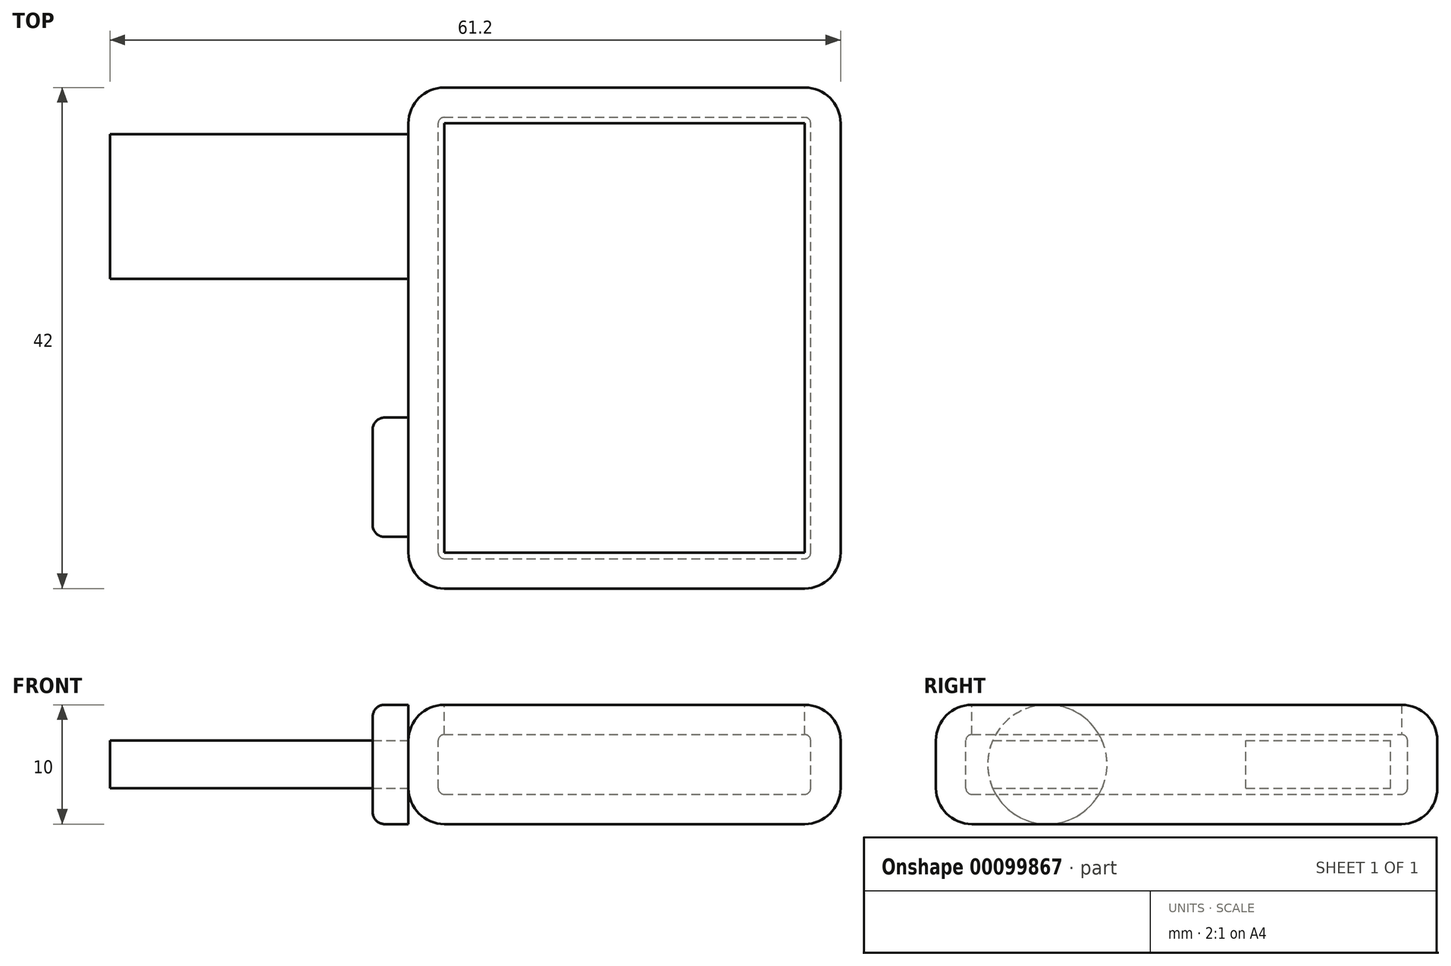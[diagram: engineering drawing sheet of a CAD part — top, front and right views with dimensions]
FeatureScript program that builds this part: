
annotation { "Feature Type Name" : "Feature", "Feature Type Description" : "" }
export const myFeature = defineFeature(function(context is Context, id is Id, definition is map)
    precondition{}
    {
        {
            var Q0;
            Q0=qCreatedBy(makeId("Top.planeOp"),FACE);
            var sketch = newSketch(context, id + "F0", { "sketchPlane" : qUnion([Q0])});
            skLineSegment(sketch, "E0.bottom", {"start": v(-18.1, -21) * mm, "end": v(18.1, -21) * mm});
            skLineSegment(sketch, "E0.top", {"start": v(-18.1, 21) * mm, "end": v(18.1, 21) * mm});
            skLineSegment(sketch, "E0.left", {"start": v(-18.1, -21) * mm, "end": v(-18.1, 21) * mm});
            skLineSegment(sketch, "E0.right", {"start": v(18.1, -21) * mm, "end": v(18.1, 21) * mm});
            skPoint(sketch, "E0.middle", {"position": v(0, 0) * mm});
            skSolve(sketch);
        }
        {
            var Q0;
            Q0=makeQuery(id+"F0.imprint","IMPRINT",FACE,{"disambiguationData":[TD([[makeQuery(id+"F0.imprint","IMPRINT",EDGE,{"derivedFrom":sQuery(id+"F0.wireOp",EDGE,"E0.bottom")}),1.0]])]});
            extrude(context, id + "F1", {"entities" : qUnion([Q0]), "depth" : 10 * mm});
        }
        {
            var Q0;
            Q0=makeQuery(id+"F1.opExtrude","SWEPT_FACE",FACE,{"disambiguationData":[OSD([sQuery(id+"F0.wireOp",EDGE,"E0.bottom")])]});
            var Q1;
            Q1=makeQuery(id+"F1.opExtrude","SWEPT_FACE",FACE,{"disambiguationData":[OSD([sQuery(id+"F0.wireOp",EDGE,"E0.left")])]});
            var Q2;
            Q2=makeQuery(id+"F1.opExtrude","SWEPT_FACE",FACE,{"disambiguationData":[OSD([sQuery(id+"F0.wireOp",EDGE,"E0.top")])]});
            var Q3;
            Q3=makeQuery(id+"F1.opExtrude","SWEPT_FACE",FACE,{"disambiguationData":[OSD([sQuery(id+"F0.wireOp",EDGE,"E0.right")])]});
            fillet(context, id + "F2", {"entities" : qUnion([Q0, Q1, Q2, Q3]), "radius" : 3 * mm, "tangentPropagation" : true, "allowEdgeOverflow" : false});
        }
        {
            var Q0;
            Q0=makeQuery(id+"F1.opExtrude","CAP_FACE",FACE,{"disambiguationData":[OSD([sQuery(id+"F0.wireOp",EDGE,"E0.bottom"),sQuery(id+"F0.wireOp",EDGE,"E0.top"),sQuery(id+"F0.wireOp",EDGE,"E0.left"),sQuery(id+"F0.wireOp",EDGE,"E0.right")])],"isStart":false});
            shell(context, id + "F3", {"entities" : qUnion([Q0]), "thickness" : 2.5 * mm});
        }
        {
            var Q0;
            Q0=makeQuery(id+"F1.opExtrude","SWEPT_FACE",FACE,{"disambiguationData":[OSD([sQuery(id+"F0.wireOp",EDGE,"E0.left")])]});
            var sketch = newSketch(context, id + "F4", { "sketchPlane" : qUnion([Q0])});
            skCircle(sketch, "E1", {"center": v(11.67, 5) * mm, "radius": 5 * mm});
            skPoint(sketch, "E1.centerSnap0", {"position": v(18, 5) * mm});
            skSolve(sketch);
        }
        {
            var Q0;
            {var subQ0=sQuery(id+"F4.wireOp",EDGE,"E1");var subQ1=sQuery(id+"F0.wireOp",EDGE,"E0.left");var subQ2=makeQuery(id+"F2.opFillet","BLEND_EDGE",EDGE,{"blendedFrom":[makeQuery(id+"F1.opExtrude","CAP_EDGE",EDGE,{"disambiguationData":[OSD([subQ1])],"isStart":true}),makeQuery(id+"F1.opExtrude","SWEPT_FACE",FACE,{"disambiguationData":[OSD([subQ1])]})],"blendedInto":[makeQuery(id+"F1.opExtrude","SWEPT_FACE",FACE,{"disambiguationData":[OSD([subQ1])]})]});var subQ3=makeQuery(id+"F4.imprint","INTERSECT",VERTEX,{"disambiguationData":[OD(0.0)],"derivedFrom":[subQ2,subQ0]});Q0=makeQuery(id+"F4.imprint","IMPRINT",FACE,{"disambiguationData":[TD([[makeQuery(id+"F4.imprint","IMPRINT",EDGE,{"disambiguationData":[TD([[subQ3,-1.0]])],"derivedFrom":subQ0}),1.0]])]});}
            var Q1;
            {var subQ0=sQuery(id+"F4.wireOp",EDGE,"E1");var subQ1=sQuery(id+"F0.wireOp",EDGE,"E0.left");var subQ2=makeQuery(id+"F1.opExtrude","SWEPT_FACE",FACE,{"disambiguationData":[OSD([subQ1])]});var subQ3=makeQuery(id+"F2.opFillet","BLEND_EDGE",EDGE,{"blendedFrom":[makeQuery(id+"F1.opExtrude","CAP_EDGE",EDGE,{"disambiguationData":[OSD([subQ1])],"isStart":false}),subQ2],"blendedInto":[subQ2]});var subQ4=makeQuery(id+"F4.imprint","INTERSECT",VERTEX,{"disambiguationData":[OD(0.0)],"derivedFrom":[subQ3,subQ0]});Q1=makeQuery(id+"F4.imprint","IMPRINT",FACE,{"disambiguationData":[TD([[makeQuery(id+"F4.imprint","IMPRINT",EDGE,{"disambiguationData":[TD([[subQ4,-1.0]])],"derivedFrom":subQ0}),1.0]])]});}
            var Q2;
            {var subQ0=sQuery(id+"F4.wireOp",EDGE,"E1");var subQ1=sQuery(id+"F0.wireOp",EDGE,"E0.left");var subQ2=makeQuery(id+"F2.opFillet","BLEND_EDGE",EDGE,{"blendedFrom":[makeQuery(id+"F1.opExtrude","CAP_EDGE",EDGE,{"disambiguationData":[OSD([subQ1])],"isStart":false}),makeQuery(id+"F1.opExtrude","SWEPT_FACE",FACE,{"disambiguationData":[OSD([subQ1])]})],"blendedInto":[makeQuery(id+"F1.opExtrude","SWEPT_FACE",FACE,{"disambiguationData":[OSD([subQ1])]})]});var subQ3=makeQuery(id+"F4.imprint","INTERSECT",VERTEX,{"disambiguationData":[OD(0.0)],"derivedFrom":[subQ2,subQ0]});Q2=makeQuery(id+"F4.imprint","IMPRINT",FACE,{"disambiguationData":[TD([[makeQuery(id+"F4.imprint","IMPRINT",EDGE,{"disambiguationData":[TD([[subQ3,1.0]])],"derivedFrom":subQ0}),1.0]])]});}
            extrude(context, id + "F5", {"entities" : qUnion([Q0, Q1, Q2]), "operationType" : NewBodyOperationType.ADD, "depth" : 3 * mm});
        }
        {
            var Q0;
            Q0=makeQuery(id+"F5.opExtrude","CAP_FACE",FACE,{"disambiguationData":[OSD([sQuery(id+"F4.wireOp",EDGE,"E1")])],"isStart":false});
            fillet(context, id + "F6", {"entities" : qUnion([Q0]), "radius" : 1 * mm, "tangentPropagation" : true, "allowEdgeOverflow" : false});
        }
        {
            var Q0;
            {var subQ1=sQuery(id+"F0.wireOp",EDGE,"E0.left");var subQ2=makeQuery(id+"F1.opExtrude","SWEPT_FACE",FACE,{"disambiguationData":[OSD([subQ1])]});var subQ7=makeQuery(id+"F2.opFillet","BLEND_EDGE",EDGE,{"blendedFrom":[makeQuery(id+"F1.opExtrude","SWEPT_EDGE",EDGE,{"disambiguationData":[OSD([sQuery(id+"F0.wireOp",EDGE,"E0.top"),subQ1])]}),subQ2],"blendedInto":[subQ2]});Q0=makeQuery(id+"F4.imprint","IMPRINT",FACE,{"disambiguationData":[TD([[makeQuery(id+"F4.imprint","IMPRINT",EDGE,{"derivedFrom":subQ7}),1.0]])]});}
            var sketch = newSketch(context, id + "F7", { "sketchPlane" : qUnion([Q0])});
            skLineSegment(sketch, "E2.bottom", {"start": v(-17.08, 2.98) * mm, "end": v(-4.96, 2.98) * mm});
            skLineSegment(sketch, "E2.top", {"start": v(-17.08, 7.01) * mm, "end": v(-4.96, 7.01) * mm});
            skLineSegment(sketch, "E2.left", {"start": v(-17.08, 2.98) * mm, "end": v(-17.08, 7.01) * mm});
            skLineSegment(sketch, "E2.right", {"start": v(-4.96, 2.98) * mm, "end": v(-4.96, 7.01) * mm});
            skSolve(sketch);
        }
        {
            var Q0;
            {var subQ0=sQuery(id+"F7.wireOp",EDGE,"E2.left");var subQ1=sQuery(id+"F0.wireOp",EDGE,"E0.left");var subQ2=makeQuery(id+"F1.opExtrude","SWEPT_FACE",FACE,{"disambiguationData":[OSD([subQ1])]});var subQ3=makeQuery(id+"F2.opFillet","BLEND_EDGE",EDGE,{"blendedFrom":[makeQuery(id+"F1.opExtrude","CAP_EDGE",EDGE,{"disambiguationData":[OSD([subQ1])],"isStart":true}),subQ2],"blendedInto":[subQ2]});var subQ5=sQuery(id+"F4.wireOp",EDGE,"E1");var subQ6=makeQuery(id+"F4.imprint","IMPRINT",EDGE,{"disambiguationData":[TD([[makeQuery(id+"F4.imprint","INTERSECT",VERTEX,{"disambiguationData":[OD(0.0)],"derivedFrom":[subQ3,subQ5]}),1.0]])],"derivedFrom":subQ3});var subQ7=makeQuery(id+"F7.imprint","INTERSECT",VERTEX,{"derivedFrom":[subQ6,subQ0]});Q0=makeQuery(id+"F7.imprint","IMPRINT",FACE,{"disambiguationData":[TD([[makeQuery(id+"F7.imprint","IMPRINT",EDGE,{"disambiguationData":[TD([[subQ7,-1.0]])],"derivedFrom":subQ0}),-1.0]])]});}
            extrude(context, id + "F8", {"entities" : qUnion([Q0]), "operationType" : NewBodyOperationType.ADD, "depth" : 25 * mm});
        }
    });
